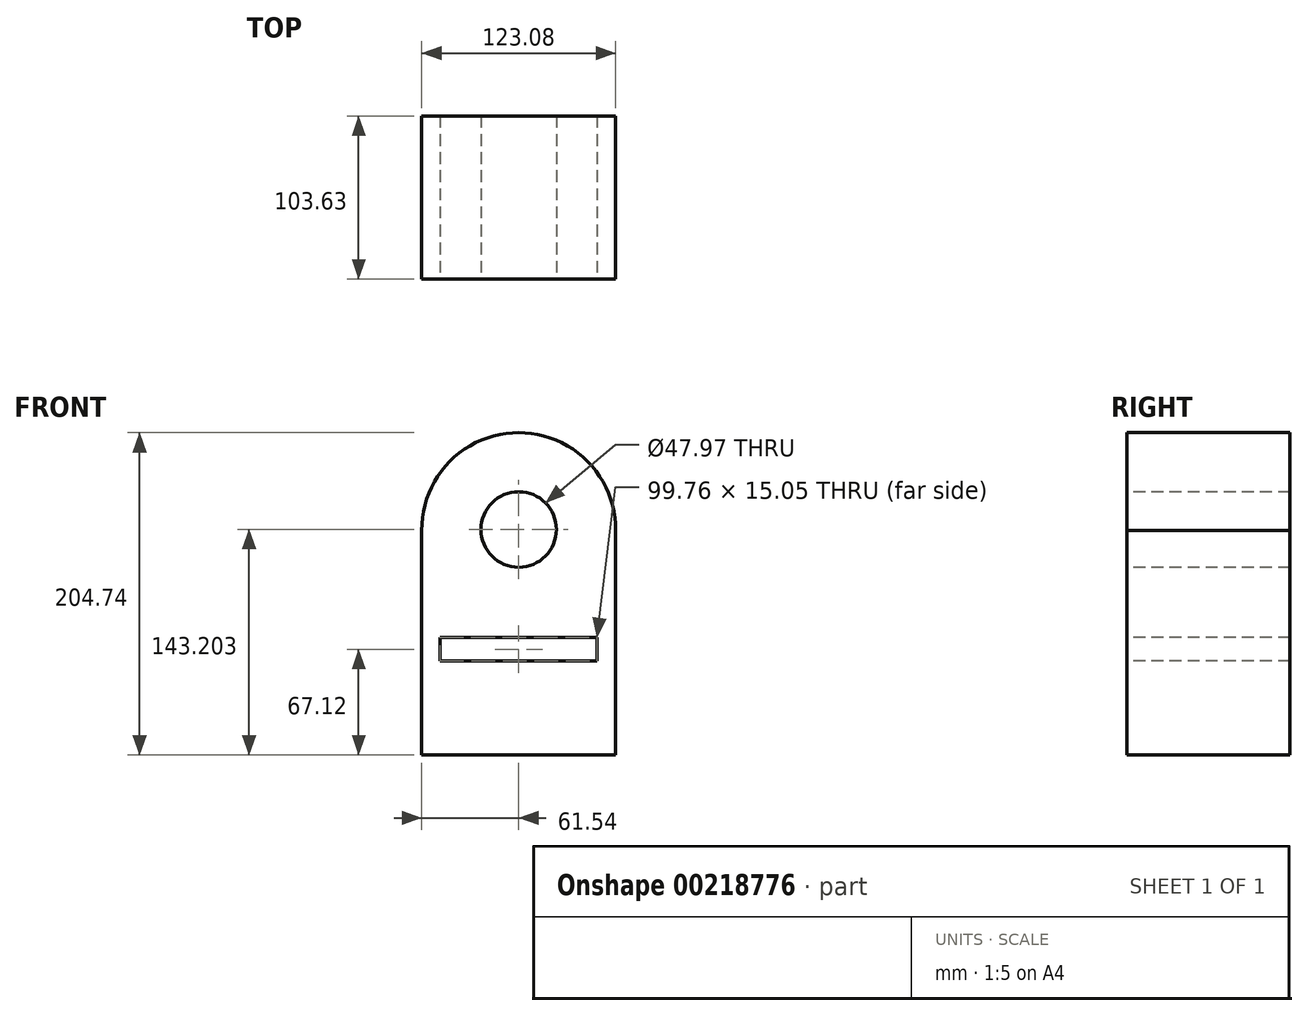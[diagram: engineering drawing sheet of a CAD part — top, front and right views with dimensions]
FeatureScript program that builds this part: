
annotation { "Feature Type Name" : "Feature", "Feature Type Description" : "" }
export const myFeature = defineFeature(function(context is Context, id is Id, definition is map)
    precondition{}
    {
        {
            var Q0;
            Q0=qCreatedBy(makeId("Front.planeOp"),FACE);
            var sketch = newSketch(context, id + "F0", { "sketchPlane" : qUnion([Q0])});
            skLineSegment(sketch, "E0.bottom", {"start": v(-61.54, -67.12) * mm, "end": v(61.54, -67.12) * mm});
            skLineSegment(sketch, "E0.top", {"start": v(-61.54, 75.38) * mm, "end": v(-61.54, 75.38) * mm});
            skLineSegment(sketch, "E0.left", {"start": v(-61.54, -67.12) * mm, "end": v(-61.54, 75.38) * mm});
            skLineSegment(sketch, "E0.right", {"start": v(61.54, -67.12) * mm, "end": v(61.54, 75.38) * mm});
            skCircle(sketch, "E1", {"center": v(0, 76.08) * mm, "radius": 23.98 * mm});
            skArc(sketch, "E2", {"start": v(61.54, 75.38) * mm, "mid": v(0, 137.62) * mm, "end": v(-61.54, 75.38) * mm});
            skLineSegment(sketch, "E3.trimOffspring", {"start": v(61.54, 75.38) * mm, "end": v(61.54, 75.38) * mm});
            skSolve(sketch);
        }
        {
            var Q0;
            Q0=makeQuery(id+"F0.imprint","IMPRINT",FACE,{"disambiguationData":[TD([[makeQuery(id+"F0.imprint","IMPRINT",EDGE,{"derivedFrom":sQuery(id+"F0.wireOp",EDGE,"E0.bottom")}),1.0]])]});
            extrude(context, id + "F1", {"entities" : qUnion([Q0]), "oppositeDirection" : true, "depth" : 103.63 * mm});
        }
        {
            var Q0;
            Q0=qCreatedBy(makeId("Front.planeOp"),FACE);
            var sketch = newSketch(context, id + "F2", { "sketchPlane" : qUnion([Q0])});
            skLineSegment(sketch, "E4.bottom", {"start": v(-49.88, 7.53) * mm, "end": v(49.88, 7.53) * mm});
            skLineSegment(sketch, "E4.top", {"start": v(-49.88, -7.53) * mm, "end": v(49.88, -7.53) * mm});
            skLineSegment(sketch, "E4.left", {"start": v(-49.88, 7.53) * mm, "end": v(-49.88, -7.53) * mm});
            skLineSegment(sketch, "E4.right", {"start": v(49.88, 7.53) * mm, "end": v(49.88, -7.53) * mm});
            skPoint(sketch, "E4.middle", {"position": v(0, 0) * mm});
            skSolve(sketch);
        }
        {
            var Q0;
            Q0=makeQuery(id+"F2.imprint","IMPRINT",FACE,{"disambiguationData":[TD([[makeQuery(id+"F2.imprint","IMPRINT",EDGE,{"derivedFrom":sQuery(id+"F2.wireOp",EDGE,"E4.bottom")}),-1.0]])]});
            extrude(context, id + "F3", {"entities" : qUnion([Q0]), "operationType" : NewBodyOperationType.REMOVE, "endBound" : BoundingType.UP_TO_NEXT, "oppositeDirection" : true, "depth" : 47.75 * mm});
        }
    });
